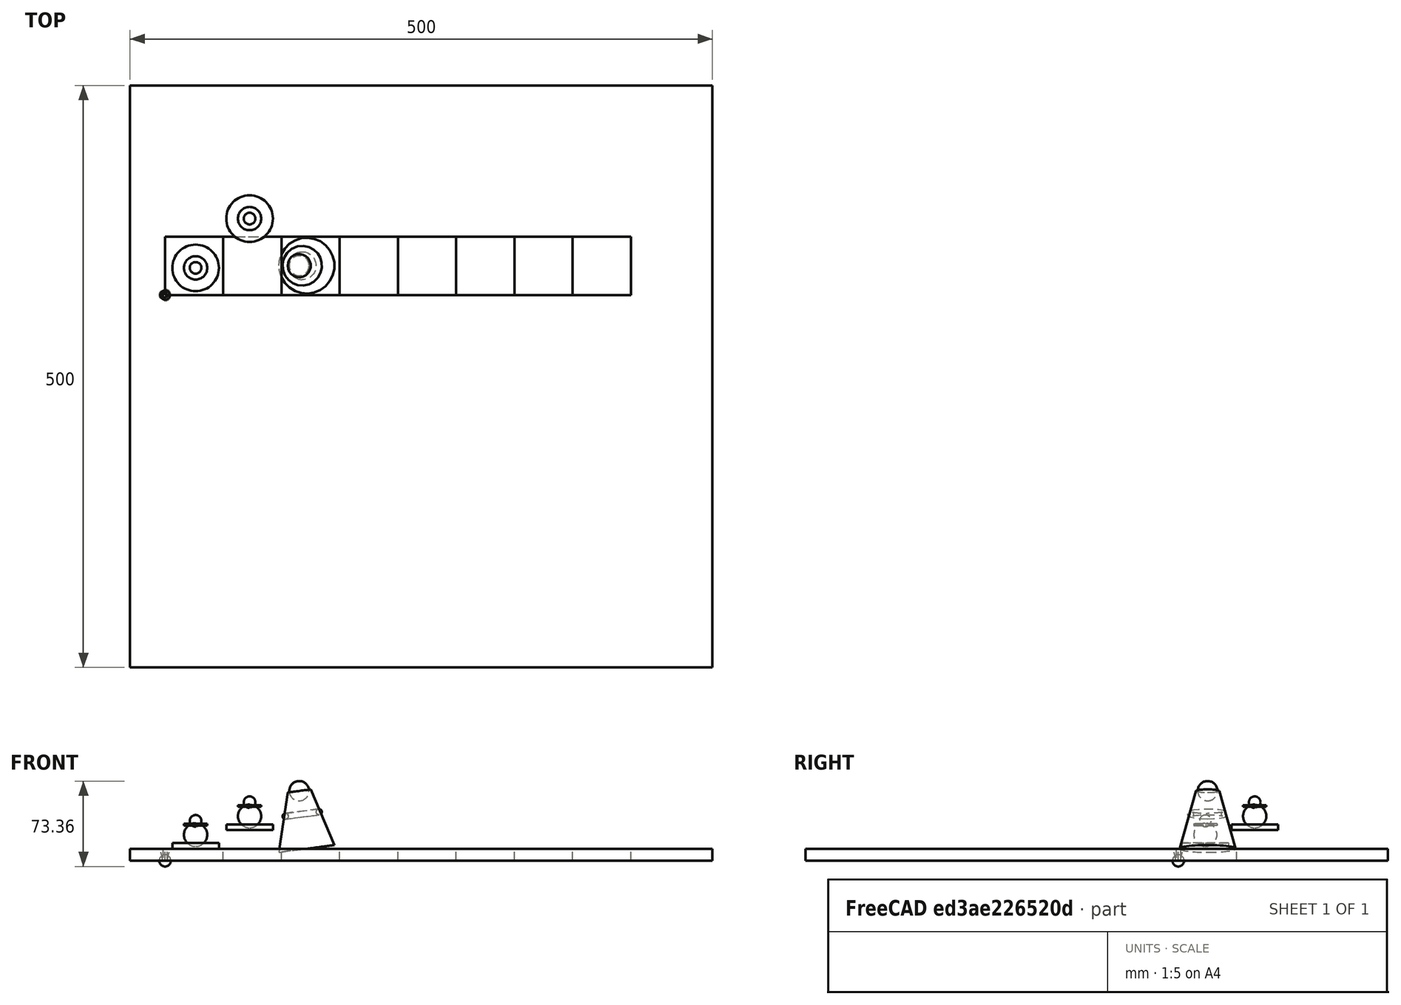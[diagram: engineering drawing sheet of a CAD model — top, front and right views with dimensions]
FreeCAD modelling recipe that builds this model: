
FCSTD DOCUMENT  (FreeCAD 0.21R33668 +26 (Git))
Label: cad
License: All rights reserved
LicenseURL: https://en.wikipedia.org/wiki/All_rights_reserved
objects: Part::Box×57, Part::Sphere×23, PartDesign::Body×8, App::Part×8, Part::Cylinder×6, App::DocumentObjectGroup×5, Part::Cone×2, Part::Torus×1
note: 97 computed .brp shape members not serialized (recipe doc carries the construction recipe); baked Part::Feature solids carry a one-line shape summary decoded from their .brp

FEATURE [PartDesign::Body] Body  label="Körper"
  Origin = -> Origin001
FEATURE [Part::Box] Box  label="Würfel"
  AttacherType = Attacher::AttachEngine3D
  Height = 10
  Length = 50
  Width = 50
FEATURE [Part::Box] Box001  label="Würfel001"
  AttacherType = Attacher::AttachEngine3D
  Height = 10
  Length = 50
  Placement = pos=(50,0,0) rot=(0,0,1;0rad)
  Width = 50
FEATURE [Part::Box] Box002  label="Würfel002"
  AttacherType = Attacher::AttachEngine3D
  Height = 10
  Length = 50
  Placement = pos=(150,0,0) rot=(0,0,1;0rad)
  Width = 50
FEATURE [Part::Box] Box003  label="Würfel003"
  AttacherType = Attacher::AttachEngine3D
  Height = 10
  Length = 50
  Placement = pos=(100,0,0) rot=(0,0,1;0rad)
  Width = 50
FEATURE [Part::Box] Box004  label="Würfel004"
  AttacherType = Attacher::AttachEngine3D
  Height = 10
  Length = 50
  Placement = pos=(200,0,0) rot=(0,0,1;0rad)
  Width = 50
FEATURE [Part::Box] Box005  label="Würfel005"
  AttacherType = Attacher::AttachEngine3D
  Height = 10
  Length = 50
  Placement = pos=(300,0,0) rot=(0,0,1;0rad)
  Width = 50
FEATURE [Part::Box] Box006  label="Würfel006"
  AttacherType = Attacher::AttachEngine3D
  Height = 10
  Length = 50
  Placement = pos=(350,0,0) rot=(0,0,1;0rad)
  Width = 50
FEATURE [Part::Box] Box007  label="Würfel007"
  AttacherType = Attacher::AttachEngine3D
  Height = 10
  Length = 50
  Placement = pos=(250,0,0) rot=(0,0,1;0rad)
  Width = 50
FEATURE [App::Part] Part  label="Row1"
  Group = -> [Body,Box,Box001,Box002,Box003,Box004,Box005,Box006,Box007]
  Origin = -> Origin
FEATURE [PartDesign::Body] Body001  label="Körper001"
  Origin = -> Origin003
FEATURE [Part::Box] Box008  label="Würfel008"
  AttacherType = Attacher::AttachEngine3D
  Height = 10
  Length = 50
  Width = 50
FEATURE [Part::Box] Box009  label="Würfel009"
  AttacherType = Attacher::AttachEngine3D
  Height = 10
  Length = 50
  Placement = pos=(50,0,0) rot=(0,0,1;0rad)
  Width = 50
FEATURE [Part::Box] Box010  label="Würfel010"
  AttacherType = Attacher::AttachEngine3D
  Height = 10
  Length = 50
  Placement = pos=(150,0,0) rot=(0,0,1;0rad)
  Width = 50
FEATURE [Part::Box] Box011  label="Würfel011"
  AttacherType = Attacher::AttachEngine3D
  Height = 10
  Length = 50
  Placement = pos=(100,0,0) rot=(0,0,1;0rad)
  Width = 50
FEATURE [Part::Box] Box012  label="Würfel012"
  AttacherType = Attacher::AttachEngine3D
  Height = 10
  Length = 50
  Placement = pos=(200,0,0) rot=(0,0,1;0rad)
  Width = 50
FEATURE [Part::Box] Box013  label="Würfel013"
  AttacherType = Attacher::AttachEngine3D
  Height = 10
  Length = 50
  Placement = pos=(300,0,0) rot=(0,0,1;0rad)
  Width = 50
FEATURE [Part::Box] Box014  label="Würfel014"
  AttacherType = Attacher::AttachEngine3D
  Height = 10
  Length = 50
  Placement = pos=(350,0,0) rot=(0,0,1;0rad)
  Width = 50
FEATURE [Part::Box] Box015  label="Würfel015"
  AttacherType = Attacher::AttachEngine3D
  Height = 10
  Length = 50
  Placement = pos=(250,0,0) rot=(0,0,1;0rad)
  Width = 50
FEATURE [App::Part] Part001  label="Row3"
  Group = -> [Body001,Box008,Box009,Box010,Box011,Box012,Box013,Box014,Box015]
  Origin = -> Origin002
  Placement = pos=(0,100,0) rot=(0,0,1;0rad)
FEATURE [PartDesign::Body] Body002  label="Körper002"
  Origin = -> Origin005
FEATURE [Part::Box] Box016  label="Würfel016"
  AttacherType = Attacher::AttachEngine3D
  Height = 10
  Length = 50
  Width = 50
FEATURE [Part::Box] Box017  label="Würfel017"
  AttacherType = Attacher::AttachEngine3D
  Height = 10
  Length = 50
  Placement = pos=(50,0,0) rot=(0,0,1;0rad)
  Width = 50
FEATURE [Part::Box] Box018  label="Würfel018"
  AttacherType = Attacher::AttachEngine3D
  Height = 10
  Length = 50
  Placement = pos=(150,0,0) rot=(0,0,1;0rad)
  Width = 50
FEATURE [Part::Box] Box019  label="Würfel019"
  AttacherType = Attacher::AttachEngine3D
  Height = 10
  Length = 50
  Placement = pos=(100,0,0) rot=(0,0,1;0rad)
  Width = 50
FEATURE [Part::Box] Box020  label="Würfel020"
  AttacherType = Attacher::AttachEngine3D
  Height = 10
  Length = 50
  Placement = pos=(200,0,0) rot=(0,0,1;0rad)
  Width = 50
FEATURE [Part::Box] Box021  label="Würfel021"
  AttacherType = Attacher::AttachEngine3D
  Height = 10
  Length = 50
  Placement = pos=(300,0,0) rot=(0,0,1;0rad)
  Width = 50
FEATURE [Part::Box] Box022  label="Würfel022"
  AttacherType = Attacher::AttachEngine3D
  Height = 10
  Length = 50
  Placement = pos=(350,0,0) rot=(0,0,1;0rad)
  Width = 50
FEATURE [Part::Box] Box023  label="Würfel023"
  AttacherType = Attacher::AttachEngine3D
  Height = 10
  Length = 50
  Placement = pos=(250,0,0) rot=(0,0,1;0rad)
  Width = 50
FEATURE [PartDesign::Body] Body003  label="Körper003"
  Origin = -> Origin007
FEATURE [Part::Box] Box024  label="Würfel024"
  AttacherType = Attacher::AttachEngine3D
  Height = 10
  Length = 50
  Width = 50
FEATURE [Part::Box] Box025  label="Würfel025"
  AttacherType = Attacher::AttachEngine3D
  Height = 10
  Length = 50
  Placement = pos=(50,0,0) rot=(0,0,1;0rad)
  Width = 50
FEATURE [Part::Box] Box026  label="Würfel026"
  AttacherType = Attacher::AttachEngine3D
  Height = 10
  Length = 50
  Placement = pos=(150,0,0) rot=(0,0,1;0rad)
  Width = 50
FEATURE [Part::Box] Box027  label="Würfel027"
  AttacherType = Attacher::AttachEngine3D
  Height = 10
  Length = 50
  Placement = pos=(100,0,0) rot=(0,0,1;0rad)
  Width = 50
FEATURE [Part::Box] Box028  label="Würfel028"
  AttacherType = Attacher::AttachEngine3D
  Height = 10
  Length = 50
  Placement = pos=(200,0,0) rot=(0,0,1;0rad)
  Width = 50
FEATURE [Part::Box] Box029  label="Würfel029"
  AttacherType = Attacher::AttachEngine3D
  Height = 10
  Length = 50
  Placement = pos=(300,0,0) rot=(0,0,1;0rad)
  Width = 50
FEATURE [Part::Box] Box030  label="Würfel030"
  AttacherType = Attacher::AttachEngine3D
  Height = 10
  Length = 50
  Placement = pos=(350,0,0) rot=(0,0,1;0rad)
  Width = 50
FEATURE [Part::Box] Box031  label="Würfel031"
  AttacherType = Attacher::AttachEngine3D
  Height = 10
  Length = 50
  Placement = pos=(250,0,0) rot=(0,0,1;0rad)
  Width = 50
FEATURE [App::Part] Part003  label="Row7"
  Group = -> [Body003,Box024,Box025,Box026,Box027,Box028,Box029,Box030,Box031]
  Origin = -> Origin006
  Placement = pos=(0,300,0) rot=(0,0,1;0rad)
FEATURE [PartDesign::Body] Body005  label="Körper005"
  Origin = -> Origin011
FEATURE [Part::Box] Box040  label="Würfel040"
  AttacherType = Attacher::AttachEngine3D
  Height = 10
  Length = 50
  Placement = pos=(50,0,0) rot=(0,0,1;0rad)
  Width = 50
FEATURE [Part::Box] Box041  label="Würfel041"
  AttacherType = Attacher::AttachEngine3D
  Height = 10
  Length = 50
  Width = 50
FEATURE [Part::Box] Box042  label="Würfel042"
  AttacherType = Attacher::AttachEngine3D
  Height = 10
  Length = 50
  Placement = pos=(100,0,0) rot=(0,0,1;0rad)
  Width = 50
FEATURE [Part::Box] Box044  label="Würfel044"
  AttacherType = Attacher::AttachEngine3D
  Height = 10
  Length = 50
  Placement = pos=(150,0,0) rot=(0,0,1;0rad)
  Width = 50
FEATURE [Part::Box] Box045  label="Würfel045"
  AttacherType = Attacher::AttachEngine3D
  Height = 10
  Length = 50
  Placement = pos=(250,0,0) rot=(0,0,1;0rad)
  Width = 50
FEATURE [Part::Box] Box046  label="Würfel046"
  AttacherType = Attacher::AttachEngine3D
  Height = 10
  Length = 50
  Placement = pos=(200,0,0) rot=(0,0,1;0rad)
  Width = 50
FEATURE [Part::Box] Box047  label="Würfel047"
  AttacherType = Attacher::AttachEngine3D
  Height = 10
  Length = 50
  Placement = pos=(300,0,0) rot=(0,0,1;0rad)
  Width = 50
FEATURE [Part::Box] Box048  label="Würfel048"
  AttacherType = Attacher::AttachEngine3D
  Height = 10
  Length = 50
  Placement = pos=(350,0,0) rot=(0,0,1;0rad)
  Width = 50
FEATURE [App::Part] Part005  label="Row2"
  Group = -> [Body005,Box040,Box041,Box042,Box044,Box045,Box046,Box047,Box048]
  Origin = -> Origin010
  Placement = pos=(0,50,0) rot=(0,0,1;0rad)
FEATURE [PartDesign::Body] Body006  label="Körper006"
  Origin = -> Origin013
FEATURE [Part::Box] Box049  label="Würfel049"
  AttacherType = Attacher::AttachEngine3D
  Height = 10
  Length = 50
  Placement = pos=(50,0,0) rot=(0,0,1;0rad)
  Width = 50
FEATURE [Part::Box] Box050  label="Würfel050"
  AttacherType = Attacher::AttachEngine3D
  Height = 10
  Length = 50
  Width = 50
FEATURE [Part::Box] Box051  label="Würfel051"
  AttacherType = Attacher::AttachEngine3D
  Height = 10
  Length = 50
  Placement = pos=(100,0,0) rot=(0,0,1;0rad)
  Width = 50
FEATURE [Part::Box] Box052  label="Würfel052"
  AttacherType = Attacher::AttachEngine3D
  Height = 10
  Length = 50
  Placement = pos=(150,0,0) rot=(0,0,1;0rad)
  Width = 50
FEATURE [Part::Box] Box053  label="Würfel053"
  AttacherType = Attacher::AttachEngine3D
  Height = 10
  Length = 50
  Placement = pos=(250,0,0) rot=(0,0,1;0rad)
  Width = 50
FEATURE [Part::Box] Box054  label="Würfel054"
  AttacherType = Attacher::AttachEngine3D
  Height = 10
  Length = 50
  Placement = pos=(200,0,0) rot=(0,0,1;0rad)
  Width = 50
FEATURE [Part::Box] Box055  label="Würfel055"
  AttacherType = Attacher::AttachEngine3D
  Height = 10
  Length = 50
  Placement = pos=(300,0,0) rot=(0,0,1;0rad)
  Width = 50
FEATURE [Part::Box] Box056  label="Würfel056"
  AttacherType = Attacher::AttachEngine3D
  Height = 10
  Length = 50
  Placement = pos=(350,0,0) rot=(0,0,1;0rad)
  Width = 50
FEATURE [App::Part] Part006  label="Row4"
  Group = -> [Body006,Box049,Box050,Box051,Box052,Box053,Box054,Box055,Box056]
  Origin = -> Origin012
  Placement = pos=(0,150,0) rot=(0,0,1;0rad)
FEATURE [PartDesign::Body] Body007  label="Körper007"
  Origin = -> Origin015
FEATURE [Part::Box] Box057  label="Würfel057"
  AttacherType = Attacher::AttachEngine3D
  Height = 10
  Length = 50
  Placement = pos=(50,0,0) rot=(0,0,1;0rad)
  Width = 50
FEATURE [Part::Box] Box058  label="Würfel058"
  AttacherType = Attacher::AttachEngine3D
  Height = 10
  Length = 50
  Width = 50
FEATURE [Part::Box] Box059  label="Würfel059"
  AttacherType = Attacher::AttachEngine3D
  Height = 10
  Length = 50
  Placement = pos=(100,0,0) rot=(0,0,1;0rad)
  Width = 50
FEATURE [Part::Box] Box060  label="Würfel060"
  AttacherType = Attacher::AttachEngine3D
  Height = 10
  Length = 50
  Placement = pos=(150,0,0) rot=(0,0,1;0rad)
  Width = 50
FEATURE [Part::Box] Box061  label="Würfel061"
  AttacherType = Attacher::AttachEngine3D
  Height = 10
  Length = 50
  Placement = pos=(250,0,0) rot=(0,0,1;0rad)
  Width = 50
FEATURE [Part::Box] Box062  label="Würfel062"
  AttacherType = Attacher::AttachEngine3D
  Height = 10
  Length = 50
  Placement = pos=(200,0,0) rot=(0,0,1;0rad)
  Width = 50
FEATURE [Part::Box] Box063  label="Würfel063"
  AttacherType = Attacher::AttachEngine3D
  Height = 10
  Length = 50
  Placement = pos=(300,0,0) rot=(0,0,1;0rad)
  Width = 50
FEATURE [Part::Box] Box064  label="Würfel064"
  AttacherType = Attacher::AttachEngine3D
  Height = 10
  Length = 50
  Placement = pos=(350,0,0) rot=(0,0,1;0rad)
  Width = 50
FEATURE [App::Part] Part007  label="Row 6"
  Group = -> [Body007,Box057,Box058,Box059,Box060,Box061,Box062,Box063,Box064]
  Origin = -> Origin014
  Placement = pos=(0,250,0) rot=(0,0,1;0rad)
FEATURE [PartDesign::Body] Body008  label="Körper008"
  Origin = -> Origin017
FEATURE [Part::Box] Box065  label="Würfel065"
  AttacherType = Attacher::AttachEngine3D
  Height = 10
  Length = 500
  Placement = pos=(-30,-320,0) rot=(0,0,1;0rad)
  Width = 500
FEATURE [App::Part] Part008  label="Board"
  Group = -> [Body008,Box065]
  Origin = -> Origin016
  Placement = pos=(-17,250,0) rot=(0,0,1;0rad)
FEATURE [Part::Sphere] Sphere  label="Kugel"
  Angle1 = -90
  Angle2 = 90
  Angle3 = 360
  AttacherType = Attacher::AttachEngine3D
  Radius = 5
FEATURE [Part::Sphere] Sphere001  label="Kugel001"
  Angle1 = -90
  Angle2 = 90
  Angle3 = 360
  AttacherType = Attacher::AttachEngine3D
  Radius = 5
FEATURE [Part::Sphere] Sphere002  label="Kugel002"
  Angle1 = -90
  Angle2 = 90
  Angle3 = 360
  AttacherType = Attacher::AttachEngine3D
  Radius = 5
FEATURE [Part::Sphere] Sphere003  label="Kugel003"
  Angle1 = -90
  Angle2 = 90
  Angle3 = 360
  AttacherType = Attacher::AttachEngine3D
  Radius = 5
FEATURE [Part::Sphere] Sphere004  label="Kugel004"
  Angle1 = -90
  Angle2 = 90
  Angle3 = 360
  AttacherType = Attacher::AttachEngine3D
  Radius = 5
FEATURE [Part::Cylinder] Cylinder  label="Zylinder"
  Angle = 360
  AttacherType = Attacher::AttachEngine3D
  FirstAngle = 0
  Height = 10
  Radius = 2
  SecondAngle = 0
FEATURE [Part::Cone] Cone  label="Kegel"
  Angle = 360
  AttacherType = Attacher::AttachEngine3D
  Height = 10
  Radius1 = 2
  Radius2 = 4
FEATURE [Part::Sphere] Sphere005  label="Kugel005"
  Angle1 = -90
  Angle2 = 90
  Angle3 = 360
  AttacherType = Attacher::AttachEngine3D
  Radius = 5
FEATURE [Part::Cylinder] Cylinder001  label="Zylinder001"
  Angle = 360
  AttacherType = Attacher::AttachEngine3D
  FirstAngle = 0
  Height = 10
  Radius = 2
  SecondAngle = 0
FEATURE [Part::Sphere] Sphere006  label="Sphere"
  Angle1 = -90
  Angle2 = 90
  Angle3 = 360
  AttacherType = Attacher::AttachEngine3D
  Radius = 5
FEATURE [Part::Sphere] Sphere007 .. Sphere017  x11 (patterned run collapsed; names and placements below)
  Angle1 = -90
  Angle2 = 90
  Angle3 = 360
  AttacherType = Attacher::AttachEngine3D
  Radius = 5
FEATURE [App::Part] Part002  label="Row5"
  Group = -> [Body002,Box016,Box017,Box018,Box019,Box020,Box021,Box022,Box023,Sphere,Sphere001,Sphere002,Sphere003,Sphere004,Cylinder,Cone,Sphere005,Cylinder001,Sphere006,Sphere007,Sphere008,Sphere009,Sphere010,Sphere011,Sphere012,Sphere013,Sphere014,Sphere015,Sphere016,Sphere017]
  Origin = -> Origin004
  Placement = pos=(0,200,0) rot=(0,0,1;0rad)
FEATURE [App::DocumentObjectGroup] Group  label="Board001"
  Group = -> [Part,Part001,Part002,Part003,Part005,Part006,Part007,Part008]
FEATURE [Part::Sphere] Sphere018
  Angle1 = -90
  Angle2 = 90
  Angle3 = 360
  AttacherType = Attacher::AttachEngine3D
  Placement = pos=(26.2312,23.2725,22.1697) rot=(0,0,1;0rad)
  Radius = 10
FEATURE [Part::Sphere] Sphere019
  Angle1 = -90
  Angle2 = 90
  Angle3 = 360
  AttacherType = Attacher::AttachEngine3D
  Placement = pos=(26.2312,23.2725,34.1697) rot=(0,0,1;0rad)
  Radius = 5
FEATURE [Part::Cylinder] Cylinder002  label="Cylinder"
  Angle = 360
  AttacherType = Attacher::AttachEngine3D
  FirstAngle = 0
  Height = 1.5
  Placement = pos=(26.2312,23.2725,30.1697) rot=(0,0,1;0rad)
  Radius = 10
  SecondAngle = 0
FEATURE [Part::Cylinder] Cylinder003
  Angle = 360
  AttacherType = Attacher::AttachEngine3D
  FirstAngle = 0
  Height = 5
  Placement = pos=(26.2312,23.2725,10.1697) rot=(0,0,1;0rad)
  Radius = 20
  SecondAngle = 0
FEATURE [App::DocumentObjectGroup] Group001  label="Pawn1"
  Group = -> [Sphere018,Sphere019,Cylinder002,Cylinder003]
FEATURE [Part::Cylinder] Cylinder004
  Angle = 360
  AttacherType = Attacher::AttachEngine3D
  FirstAngle = 0
  Height = 1.5
  Placement = pos=(72.5767,65.6147,46.195) rot=(0,0,1;0rad)
  Radius = 10
  SecondAngle = 0
FEATURE [Part::Cylinder] Cylinder005
  Angle = 360
  AttacherType = Attacher::AttachEngine3D
  FirstAngle = 0
  Height = 5
  Placement = pos=(72.5767,65.6147,26.195) rot=(0,0,1;0rad)
  Radius = 20
  SecondAngle = 0
FEATURE [Part::Sphere] Sphere020
  Angle1 = -90
  Angle2 = 90
  Angle3 = 360
  AttacherType = Attacher::AttachEngine3D
  Placement = pos=(72.5767,65.6147,38.195) rot=(0,0,1;0rad)
  Radius = 10
FEATURE [Part::Sphere] Sphere021
  Angle1 = -90
  Angle2 = 90
  Angle3 = 360
  AttacherType = Attacher::AttachEngine3D
  Placement = pos=(72.5767,65.6147,50.195) rot=(0,0,1;0rad)
  Radius = 5
FEATURE [App::DocumentObjectGroup] Group002  label="Pawn2"
  Group = -> [Sphere020,Sphere021,Cylinder004,Cylinder005]
FEATURE [Part::Cone] Cone001  label="Cone"
  Angle = 360
  AttacherType = Attacher::AttachEngine3D
  Height = 50
  Placement = pos=(115.187,25.1761,59.8605) rot=(0,1,-1e-06;3.01173rad)
  Radius1 = 10
  Radius2 = 24
FEATURE [Part::Sphere] Sphere022
  Angle1 = -90
  Angle2 = 90
  Angle3 = 360
  AttacherType = Attacher::AttachEngine3D
  Placement = pos=(115.187,25.1761,59.8605) rot=(0,1,-1e-06;3.01173rad)
  Radius = 8.5
FEATURE [Part::Torus] Torus
  Angle1 = -180
  Angle2 = 180
  Angle3 = 360
  AttacherType = Attacher::AttachEngine3D
  Placement = pos=(117.777,25.1761,40.0289) rot=(0,1,-1e-06;3.01173rad)
  Radius1 = 14.5
  Radius2 = 2.5
FEATURE [App::DocumentObjectGroup] Group003  label="Bishop"
  Group = -> [Cone001,Sphere022,Torus]
FEATURE [App::DocumentObjectGroup] Group004  label="Figures"
  Group = -> [Group003,Group002,Group001]
